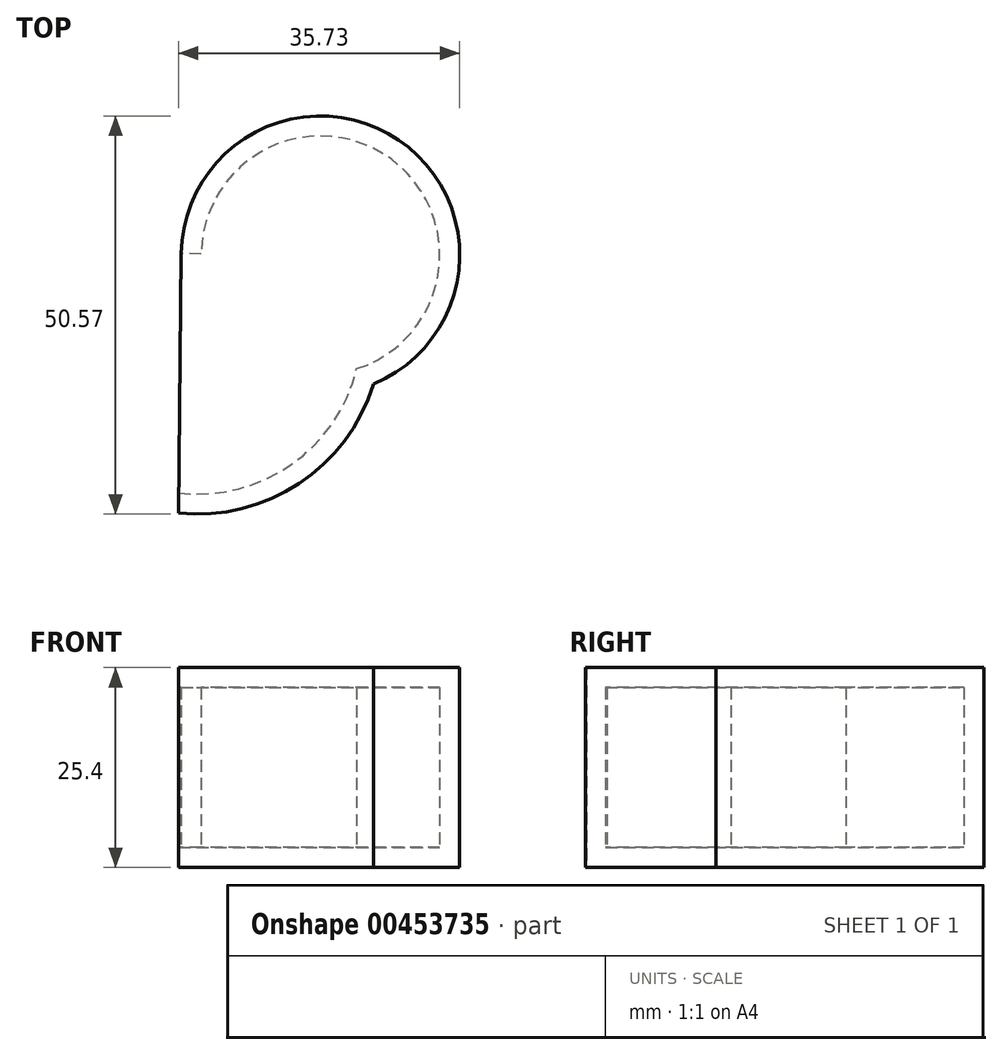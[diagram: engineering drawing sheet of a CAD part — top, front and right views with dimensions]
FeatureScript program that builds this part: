
annotation { "Feature Type Name" : "Feature", "Feature Type Description" : "" }
export const myFeature = defineFeature(function(context is Context, id is Id, definition is map)
    precondition{}
    {
        {
            var Q0;
            Q0=qCreatedBy(makeId("Top.planeOp"),FACE);
            var sketch = newSketch(context, id + "F0", { "sketchPlane" : qUnion([Q0])});
            skLineSegment(sketch, "E0", {"start": v(-12.01, 22.02) * mm, "end": v(-12.38, -10.94) * mm});
            skArc(sketch, "E1", {"start": v(12.38, 5.47) * mm, "mid": v(15.6, 36.46) * mm, "end": v(-12.01, 22.02) * mm});
            skArc(sketch, "E2", {"start": v(-12.38, -10.94) * mm, "mid": v(2.95, -7.18) * mm, "end": v(12.38, 5.47) * mm});
            skSolve(sketch);
        }
        {
            var Q0;
            Q0=makeQuery(id+"F0.imprint","IMPRINT",FACE,{"disambiguationData":[TD([[makeQuery(id+"F0.imprint","IMPRINT",EDGE,{"derivedFrom":sQuery(id+"F0.wireOp",EDGE,"E0")}),1.0]])]});
            extrude(context, id + "F1", {"entities" : qUnion([Q0]), "depth" : 25.4 * mm});
        }
        {
            var Q0;
            Q0=makeQuery(id+"F1.opExtrude","SWEPT_FACE",FACE,{"disambiguationData":[OSD([sQuery(id+"F0.wireOp",EDGE,"E0")])]});
            shell(context, id + "F2", {"entities" : qUnion([Q0]), "thickness" : 2.54 * mm});
        }
    });
